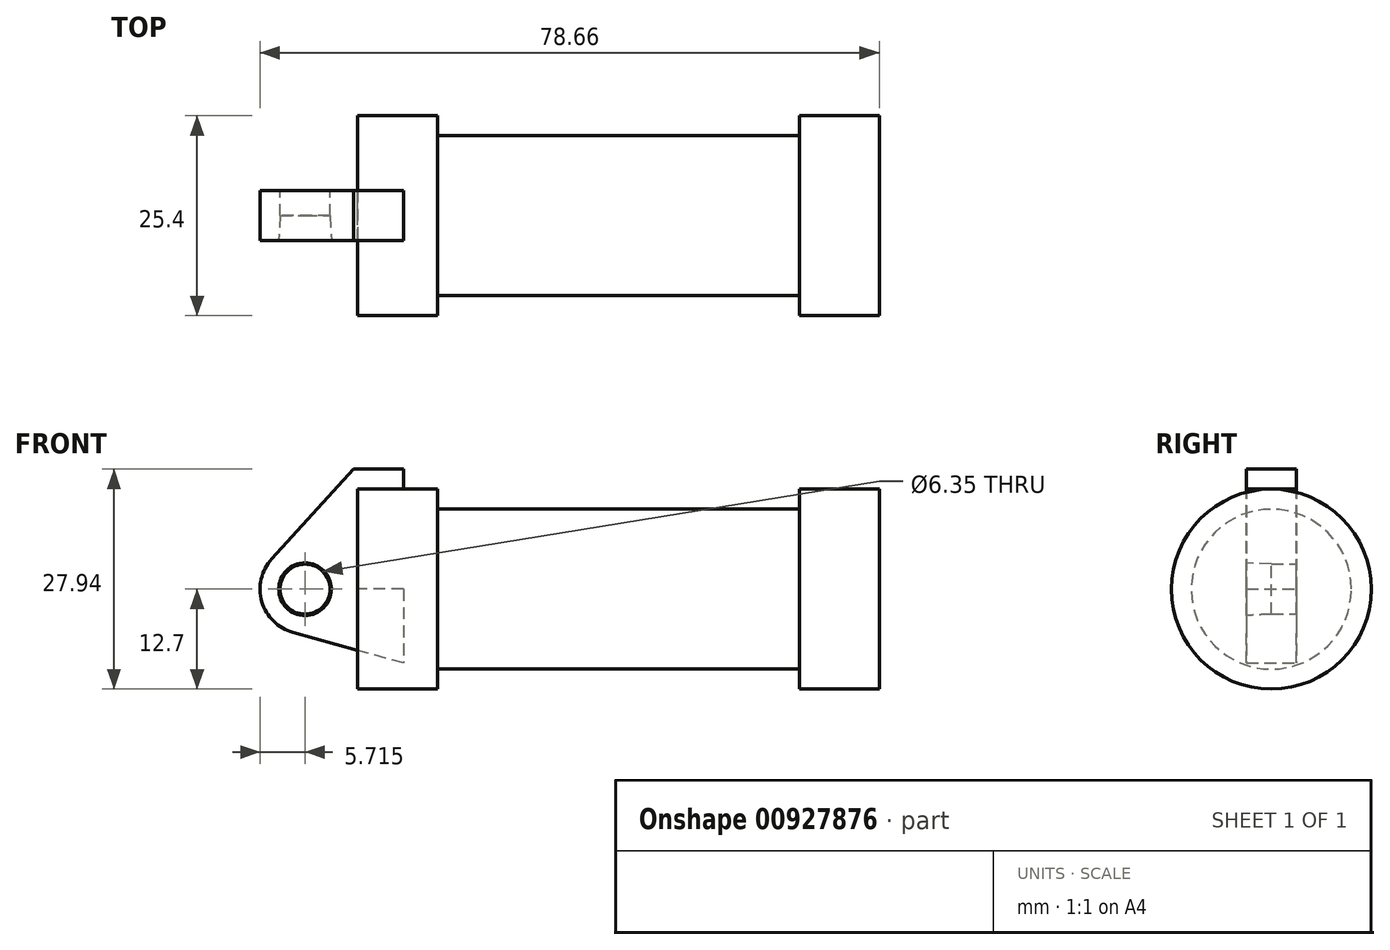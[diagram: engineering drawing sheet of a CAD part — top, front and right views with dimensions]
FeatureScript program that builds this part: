
annotation { "Feature Type Name" : "Feature", "Feature Type Description" : "" }
export const myFeature = defineFeature(function(context is Context, id is Id, definition is map)
    precondition{}
    {
        {
            var Q0;
            Q0=qCreatedBy(makeId("Front.planeOp"),FACE);
            var sketch = newSketch(context, id + "F0", { "sketchPlane" : qUnion([Q0])});
            skLineSegment(sketch, "E0", {"start": v(0, 0) * mm, "end": v(0, 12.7) * mm});
            skLineSegment(sketch, "E1", {"start": v(0, 12.7) * mm, "end": v(10.16, 12.7) * mm});
            skLineSegment(sketch, "E2", {"start": v(10.16, 12.7) * mm, "end": v(10.16, 10.16) * mm});
            skLineSegment(sketch, "E3", {"start": v(10.16, 10.16) * mm, "end": v(56.13, 10.16) * mm});
            skLineSegment(sketch, "E4", {"start": v(56.13, 10.16) * mm, "end": v(56.13, 12.7) * mm});
            skLineSegment(sketch, "E5", {"start": v(56.13, 12.7) * mm, "end": v(66.3, 12.7) * mm});
            skLineSegment(sketch, "E6", {"start": v(66.3, 12.7) * mm, "end": v(66.3, 0) * mm});
            skLineSegment(sketch, "E7", {"start": v(66.3, 0) * mm, "end": v(0, 0) * mm});
            skLineSegment(sketch, "E8", {"start": v(5.84, 15.24) * mm, "end": v(-0.5, 15.24) * mm});
            skLineSegment(sketch, "E9", {"start": v(-0.5, 15.24) * mm, "end": v(-10.88, 3.85) * mm});
            skLineSegment(sketch, "E10", {"start": v(0, 0) * mm, "end": v(-6.65, 0) * mm});
            skCircle(sketch, "E11", {"center": v(-6.65, 0) * mm, "radius": 5.72 * mm});
            skCircle(sketch, "E12", {"center": v(-6.65, 0) * mm, "radius": 3.18 * mm});
            skLineSegment(sketch, "E13", {"start": v(5.84, 15.24) * mm, "end": v(5.84, -9.4) * mm});
            skLineSegment(sketch, "E14", {"start": v(5.84, -9.4) * mm, "end": v(-8.18, -5.5) * mm});
            skSolve(sketch);
        }
        {
            var Q0;
            {var subQ1=sQuery(id+"F0.wireOp",EDGE,"E0");Q0=makeQuery(id+"F0.imprint","IMPRINT",FACE,{"disambiguationData":[TD([[makeQuery(id+"F0.imprint","IMPRINT",EDGE,{"derivedFrom":subQ1}),1.0]])]});}
            var Q1;
            {var subQ0=sQuery(id+"F0.wireOp",EDGE,"E14");Q1=makeQuery(id+"F0.imprint","IMPRINT",FACE,{"disambiguationData":[TD([[makeQuery(id+"F0.imprint","IMPRINT",EDGE,{"derivedFrom":subQ0}),-1.0]])]});}
            var Q2;
            {var subQ5=sQuery(id+"F0.wireOp",EDGE,"E12");Q2=makeQuery(id+"F0.imprint","IMPRINT",FACE,{"disambiguationData":[TD([[makeQuery(id+"F0.imprint","IMPRINT",EDGE,{"derivedFrom":subQ5}),-1.0]])]});}
            var Q3;
            {var subQ0=sQuery(id+"F0.wireOp",EDGE,"E12");Q3=makeQuery(id+"F0.imprint","IMPRINT",FACE,{"disambiguationData":[TD([[makeQuery(id+"F0.imprint","IMPRINT",EDGE,{"derivedFrom":subQ0}),1.0]])]});}
            extrude(context, id + "F1", {"entities" : qUnion([Q0, Q1, Q2, Q3]), "depth" : 3.17 * mm, "offsetDistance" : 25.4 * mm, "hasSecondDirection" : true, "secondDirectionOppositeDirection" : true, "secondDirectionDepth" : 3.17 * mm});
        }
        {
            var Q0;
            {var subQ0=sQuery(id+"F0.wireOp",EDGE,"E12");Q0=makeQuery(id+"F0.imprint","IMPRINT",FACE,{"disambiguationData":[TD([[makeQuery(id+"F0.imprint","IMPRINT",EDGE,{"derivedFrom":subQ0}),1.0]])]});}
            extrude(context, id + "F2", {"entities" : qUnion([Q0]), "operationType" : NewBodyOperationType.REMOVE, "endBound" : BoundingType.THROUGH_ALL, "depth" : 0.5 * mm, "offsetDistance" : 25.4 * mm, "hasDraft" : true, "draftAngle" : 3 * degree, "hasSecondDirection" : true, "secondDirectionBound" : SecondDirectionBoundingType.THROUGH_ALL, "secondDirectionOppositeDirection" : true, "secondDirectionDepth" : 25.4 * mm});
        }
        {
            var Q0;
            {var subQ0=sQuery(id+"F0.wireOp",EDGE,"E0");Q0=makeQuery(id+"F0.imprint","IMPRINT",FACE,{"disambiguationData":[TD([[makeQuery(id+"F0.imprint","IMPRINT",EDGE,{"derivedFrom":subQ0}),-1.0]])]});}
            var Q1;
            {var subQ0=sQuery(id+"F0.wireOp",EDGE,"E2");Q1=makeQuery(id+"F0.imprint","IMPRINT",FACE,{"disambiguationData":[TD([[makeQuery(id+"F0.imprint","IMPRINT",EDGE,{"derivedFrom":subQ0}),-1.0]])]});}
            var Q2;
            Q2=sQuery(id+"F0.wireOp",EDGE,"E7");
            revolve(context, id + "F3", {"surfaceOperationType" : NewSurfaceOperationType.NEW, "entities" : qUnion([Q0, Q1]), "axis" : qUnion([Q2]), "revolveType" : RevolveType.FULL});
        }
    });
